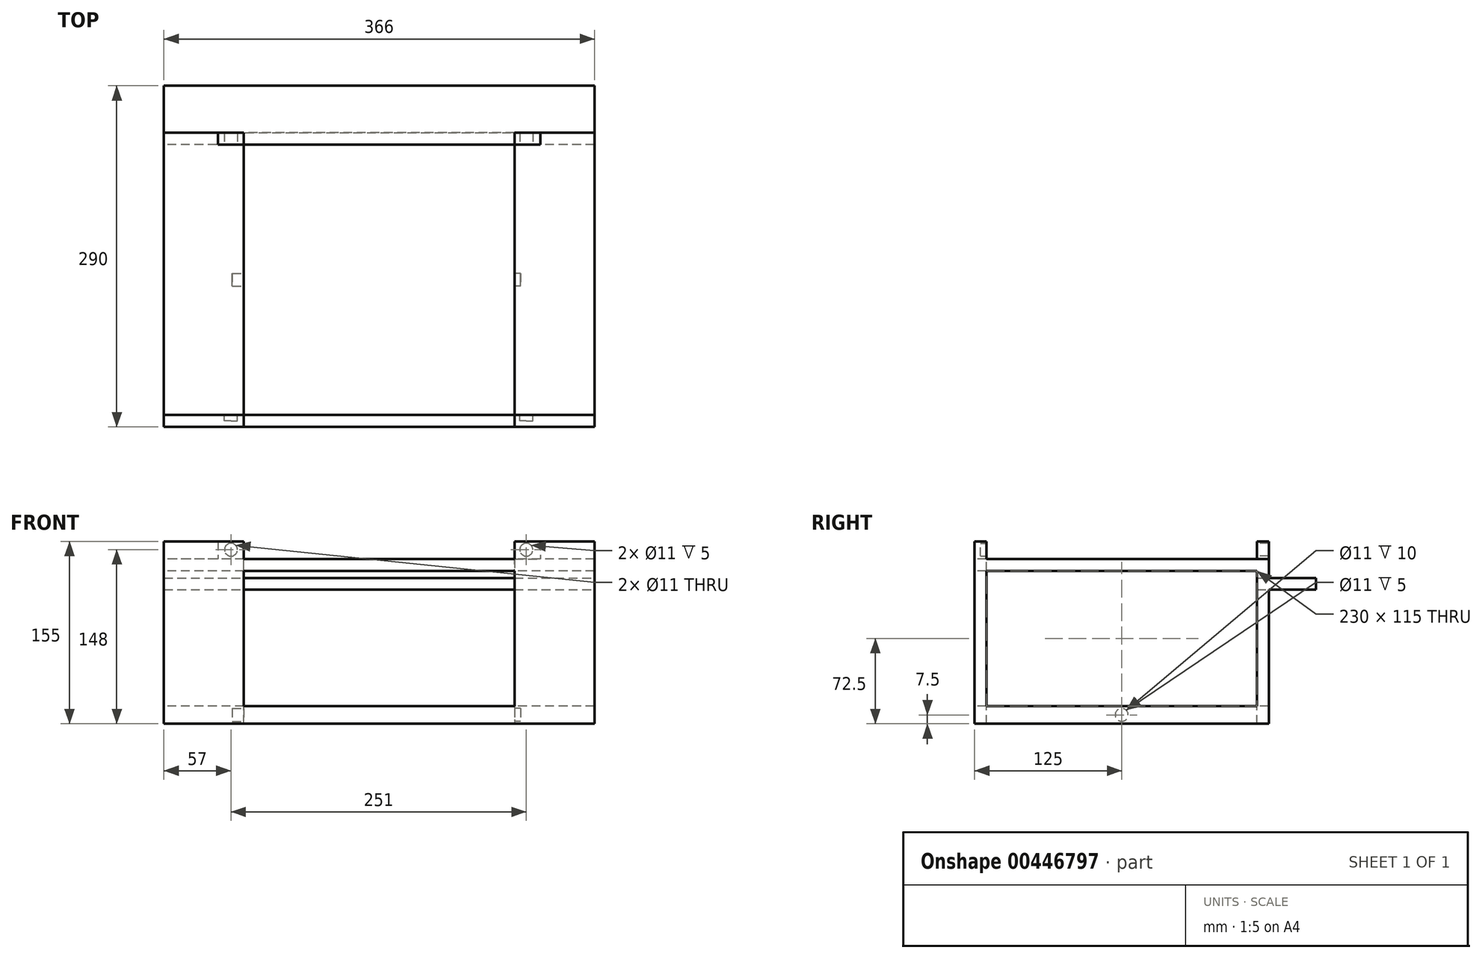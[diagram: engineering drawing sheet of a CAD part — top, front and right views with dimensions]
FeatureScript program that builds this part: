
annotation { "Feature Type Name" : "Feature", "Feature Type Description" : "" }
export const myFeature = defineFeature(function(context is Context, id is Id, definition is map)
    precondition{}
    {
        {
            var Q0;
            Q0=qCreatedBy(makeId("Top.planeOp"),FACE);
            var sketch = newSketch(context, id + "F0", { "sketchPlane" : qUnion([Q0])});
            skLineSegment(sketch, "E0.bottom", {"start": v(-183, 125) * mm, "end": v(183, 125) * mm});
            skLineSegment(sketch, "E0.top", {"start": v(-183, -125) * mm, "end": v(183, -125) * mm});
            skLineSegment(sketch, "E0.left", {"start": v(-183, 125) * mm, "end": v(-183, -125) * mm});
            skLineSegment(sketch, "E0.right", {"start": v(183, 125) * mm, "end": v(183, -125) * mm});
            skSolve(sketch);
        }
        {
            var Q0;
            Q0=qSketchRegion(id+"F0",true);
            extrude(context, id + "F1", {"entities" : qUnion([Q0]), "depth" : 155 * mm});
        }
        {
            var Q0;
            Q0=makeQuery(id+"F1.opExtrude","CAP_FACE",FACE,{"disambiguationData":[OSD([sQuery(id+"F0.wireOp",EDGE,"E0.bottom"),sQuery(id+"F0.wireOp",EDGE,"E0.top"),sQuery(id+"F0.wireOp",EDGE,"E0.left"),sQuery(id+"F0.wireOp",EDGE,"E0.right")])],"isStart":false});
            shell(context, id + "F2", {"entities" : qUnion([Q0]), "thickness" : 10 * mm});
        }
        {
            var Q0;
            Q0=makeQuery(id+"F2.opShell","OFFSET_FACE",FACE,{"disambiguationData":[OSD([sQuery(id+"F0.wireOp",EDGE,"E0.bottom"),sQuery(id+"F0.wireOp",EDGE,"E0.top"),sQuery(id+"F0.wireOp",EDGE,"E0.left"),sQuery(id+"F0.wireOp",EDGE,"E0.right")])]});
            var sketch = newSketch(context, id + "F3", { "sketchPlane" : qUnion([Q0])});
            skSolve(sketch);
        }
        {
            var Q0;
            Q0=qSketchRegion(id+"F3",true);
            var Q1;
            {var subQ0=sQuery(id+"F0.wireOp",EDGE,"E0.bottom");Q1=makeQuery(id+"F3.imprint","IMPRINT",FACE,{"disambiguationData":[TD([[makeQuery(id+"F3.imprint","IMPRINT",EDGE,{"derivedFrom":makeQuery(id+"F2.opShell","OFFSET_EDGE",EDGE,{"disambiguationData":[OSD([subQ0]),TDD([makeQuery(id+"F1.opExtrude","CAP_EDGE",EDGE,{"disambiguationData":[OSD([subQ0])],"isStart":true})])]})}),-1.0]])]});}
            extrude(context, id + "F4", {"entities" : qUnion([Q0, Q1]), "operationType" : NewBodyOperationType.REMOVE, "oppositeDirection" : true, "depth" : 25 * mm});
        }
        {
            var Q0;
            Q0=makeQuery(id+"F1.opExtrude","SWEPT_FACE",FACE,{"disambiguationData":[OSD([sQuery(id+"F0.wireOp",EDGE,"E0.top")])]});
            var sketch = newSketch(context, id + "F5", { "sketchPlane" : qUnion([Q0])});
            skLineSegment(sketch, "E1", {"start": v(0, 0) * mm, "end": v(0, 92.09) * mm});
            skLineSegment(sketch, "E2.bottom", {"start": v(-115, 130) * mm, "end": v(115, 130) * mm});
            skLineSegment(sketch, "E2.top", {"start": v(-115, 15) * mm, "end": v(115, 15) * mm});
            skLineSegment(sketch, "E2.left", {"start": v(-115, 130) * mm, "end": v(-115, 15) * mm});
            skLineSegment(sketch, "E2.right", {"start": v(115, 130) * mm, "end": v(115, 15) * mm});
            skLineSegment(sketch, "E3.bottom", {"start": v(-115, 155) * mm, "end": v(115, 155) * mm});
            skLineSegment(sketch, "E3.top", {"start": v(-115, 140) * mm, "end": v(115, 140) * mm});
            skLineSegment(sketch, "E3.left", {"start": v(-115, 155) * mm, "end": v(-115, 140) * mm});
            skLineSegment(sketch, "E3.right", {"start": v(115, 155) * mm, "end": v(115, 140) * mm});
            skSolve(sketch);
        }
        {
            var Q0;
            Q0=qSketchRegion(id+"F5",true);
            extrude(context, id + "F6", {"entities" : qUnion([Q0]), "operationType" : NewBodyOperationType.REMOVE, "oppositeDirection" : true, "depth" : 500 * mm});
        }
        {
            var Q0;
            Q0=makeQuery(id+"F1.opExtrude","SWEPT_FACE",FACE,{"disambiguationData":[OSD([sQuery(id+"F0.wireOp",EDGE,"E0.left")])]});
            var sketch = newSketch(context, id + "F7", { "sketchPlane" : qUnion([Q0])});
            skLineSegment(sketch, "E4", {"start": v(0, 0) * mm, "end": v(0, 112.83) * mm});
            skLineSegment(sketch, "E5.bottom", {"start": v(-115, 130) * mm, "end": v(115, 130) * mm});
            skLineSegment(sketch, "E5.top", {"start": v(-115, 15) * mm, "end": v(115, 15) * mm});
            skLineSegment(sketch, "E5.left", {"start": v(-115, 130) * mm, "end": v(-115, 15) * mm});
            skLineSegment(sketch, "E5.right", {"start": v(115, 130) * mm, "end": v(115, 15) * mm});
            skLineSegment(sketch, "E6.bottom", {"start": v(-125, 114) * mm, "end": v(-125, 114) * mm});
            skLineSegment(sketch, "E6.top", {"start": v(-125, 0) * mm, "end": v(-125, 0) * mm});
            skLineSegment(sketch, "E7.bottom", {"start": v(-125, 155) * mm, "end": v(115, 155) * mm});
            skLineSegment(sketch, "E7.top", {"start": v(-125, 140) * mm, "end": v(115, 140) * mm});
            skLineSegment(sketch, "E7.left", {"start": v(-125, 155) * mm, "end": v(-125, 140) * mm});
            skLineSegment(sketch, "E7.right", {"start": v(115, 155) * mm, "end": v(115, 140) * mm});
            skSolve(sketch);
        }
        {
            var Q0;
            Q0=makeQuery(id+"F7.imprint","IMPRINT",FACE,{"disambiguationData":[TD([[makeQuery(id+"F7.imprint","IMPRINT",EDGE,{"derivedFrom":sQuery(id+"F7.wireOp",EDGE,"E7.bottom")}),-1.0]])]});
            var Q1;
            Q1=makeQuery(id+"F7.imprint","IMPRINT",FACE,{"disambiguationData":[TD([[makeQuery(id+"F7.imprint","IMPRINT",EDGE,{"derivedFrom":sQuery(id+"F7.wireOp",EDGE,"E5.bottom")}),-1.0]])]});
            extrude(context, id + "F8", {"entities" : qUnion([Q0, Q1]), "operationType" : NewBodyOperationType.REMOVE, "oppositeDirection" : true, "depth" : 500 * mm});
        }
        {
            var Q0;
            Q0=makeQuery(id+"F1.opExtrude","SWEPT_FACE",FACE,{"disambiguationData":[OSD([sQuery(id+"F0.wireOp",EDGE,"E0.left")])]});
            var sketch = newSketch(context, id + "F9", { "sketchPlane" : qUnion([Q0])});
            skLineSegment(sketch, "E8.bottom", {"start": v(-115, 124) * mm, "end": v(-165, 124) * mm});
            skLineSegment(sketch, "E8.top", {"start": v(-115, 114) * mm, "end": v(-165, 114) * mm});
            skLineSegment(sketch, "E8.left", {"start": v(-115, 124) * mm, "end": v(-115, 114) * mm});
            skLineSegment(sketch, "E8.right", {"start": v(-165, 124) * mm, "end": v(-165, 114) * mm});
            skLineSegment(sketch, "E9.0", {"start": v(115, 155) * mm, "end": v(125, 155) * mm});
            skLineSegment(sketch, "E10.0", {"start": v(125, 155) * mm, "end": v(125, 0) * mm});
            skSolve(sketch);
        }
        {
            var Q0;
            Q0=qSketchRegion(id+"F9",true);
            var Q1;
            Q1=makeQuery(id+"F1.opExtrude","SWEPT_FACE",FACE,{"disambiguationData":[OSD([sQuery(id+"F0.wireOp",EDGE,"E0.right")])]});
            extrude(context, id + "F10", {"entities" : qUnion([Q0]), "operationType" : NewBodyOperationType.ADD, "endBound" : BoundingType.UP_TO_SURFACE, "oppositeDirection" : true, "endBoundEntityFace" : qUnion([Q1]), "depth" : 25 * mm});
        }
        {
            var Q0;
            {var subQ0=sQuery(id+"F0.wireOp",EDGE,"E0.bottom");var subQ1=makeQuery(id+"F1.opExtrude","SWEPT_FACE",FACE,{"disambiguationData":[OSD([subQ0])]});var subQ9=sQuery(id+"F9.wireOp",EDGE,"E8.bottom");Q0=makeQuery(id+"F10.boolean.opBoolean","SPLIT",FACE,{"disambiguationData":[TD([makeQuery(id+"F10.opExtrude","SWEPT_FACE",FACE,{"disambiguationData":[OSD([subQ9])]})])],"derivedFrom":subQ1});}
            var sketch = newSketch(context, id + "F11", { "sketchPlane" : qUnion([Q0])});
            skLineSegment(sketch, "E11.bottom", {"start": v(-115, 124) * mm, "end": v(115, 124) * mm});
            skLineSegment(sketch, "E11.top", {"start": v(-115, 150.02) * mm, "end": v(115, 150.02) * mm});
            skLineSegment(sketch, "E11.left", {"start": v(-115, 124) * mm, "end": v(-115, 150.02) * mm});
            skLineSegment(sketch, "E11.right", {"start": v(115, 124) * mm, "end": v(115, 150.02) * mm});
            skSolve(sketch);
        }
        {
            var Q0;
            {var subQ0=sQuery(id+"F11.wireOp",EDGE,"E11.bottom");Q0=makeQuery(id+"F11.imprint","IMPRINT",FACE,{"disambiguationData":[TD([[makeQuery(id+"F11.imprint","IMPRINT",EDGE,{"derivedFrom":subQ0}),1.0]])]});}
            var Q1;
            {var subQ1=sQuery(id+"F0.wireOp",EDGE,"E0.bottom");var subQ2=makeQuery(id+"F1.opExtrude","SWEPT_FACE",FACE,{"disambiguationData":[OSD([subQ1])]});var subQ3=makeQuery(id+"F6.boolean.opBoolean","INTERSECT",EDGE,{"derivedFrom":[subQ2,makeQuery(id+"F6.opExtrude","SWEPT_FACE",FACE,{"disambiguationData":[OSD([sQuery(id+"F5.wireOp",EDGE,"E2.bottom")])]})]});Q1=makeQuery(id+"F11.imprint","IMPRINT",FACE,{"disambiguationData":[TD([[makeQuery(id+"F11.imprint","IMPRINT",EDGE,{"derivedFrom":subQ3}),1.0]])]});}
            extrude(context, id + "F12", {"entities" : qUnion([Q0, Q1]), "operationType" : NewBodyOperationType.REMOVE, "oppositeDirection" : true, "depth" : 200 * mm});
        }
        {
            var Q0;
            {var subQ0=sQuery(id+"F0.wireOp",EDGE,"E0.right");var subQ2=sQuery(id+"F0.wireOp",EDGE,"E0.bottom");var subQ4=makeQuery(id+"F1.opExtrude","SWEPT_FACE",FACE,{"disambiguationData":[OSD([subQ2])]});Q0=makeQuery(id+"F12.boolean.opBoolean","SPLIT",FACE,{"disambiguationData":[TD([makeQuery(id+"F1.opExtrude","SWEPT_FACE",FACE,{"disambiguationData":[OSD([subQ0])]})])],"derivedFrom":makeQuery(id+"F8.boolean.opBoolean","MERGE",FACE,{"derivedFrom":[makeQuery(id+"F6.boolean.opBoolean","COPY",FACE,{"disambiguationData":[TD([subQ4])],"derivedFrom":makeQuery(id+"F6.opExtrude","SWEPT_FACE",FACE,{"disambiguationData":[OSD([sQuery(id+"F5.wireOp",EDGE,"E3.top")])]})}),makeQuery(id+"F8.opExtrude","SWEPT_FACE",FACE,{"disambiguationData":[OSD([sQuery(id+"F7.wireOp",EDGE,"E7.top")])]})]})});}
            var sketch = newSketch(context, id + "F13", { "sketchPlane" : qUnion([Q0])});
            skLineSegment(sketch, "E12.bottom", {"start": v(115, 115) * mm, "end": v(137, 115) * mm});
            skLineSegment(sketch, "E12.top", {"start": v(115, 125) * mm, "end": v(137, 125) * mm});
            skLineSegment(sketch, "E12.left", {"start": v(115, 115) * mm, "end": v(115, 125) * mm});
            skLineSegment(sketch, "E12.right", {"start": v(137, 115) * mm, "end": v(137, 125) * mm});
            skSolve(sketch);
        }
        {
            var Q0;
            Q0=makeQuery(id+"F13.imprint","IMPRINT",FACE,{"disambiguationData":[TD([[makeQuery(id+"F13.imprint","IMPRINT",EDGE,{"derivedFrom":sQuery(id+"F13.wireOp",EDGE,"E12.bottom")}),-1.0]])]});
            extrude(context, id + "F14", {"entities" : qUnion([Q0]), "operationType" : NewBodyOperationType.ADD, "depth" : 15 * mm});
        }
        {
            var Q0;
            {var subQ0=sQuery(id+"F0.wireOp",EDGE,"E0.bottom");var subQ3=makeQuery(id+"F1.opExtrude","SWEPT_FACE",FACE,{"disambiguationData":[OSD([subQ0])]});var subQ4=sQuery(id+"F0.wireOp",EDGE,"E0.left");Q0=makeQuery(id+"F12.boolean.opBoolean","SPLIT",FACE,{"disambiguationData":[TD([makeQuery(id+"F1.opExtrude","SWEPT_FACE",FACE,{"disambiguationData":[OSD([subQ4])]})])],"derivedFrom":makeQuery(id+"F8.boolean.opBoolean","MERGE",FACE,{"derivedFrom":[makeQuery(id+"F6.boolean.opBoolean","COPY",FACE,{"disambiguationData":[TD([subQ3])],"derivedFrom":makeQuery(id+"F6.opExtrude","SWEPT_FACE",FACE,{"disambiguationData":[OSD([sQuery(id+"F5.wireOp",EDGE,"E3.top")])]})}),makeQuery(id+"F8.opExtrude","SWEPT_FACE",FACE,{"disambiguationData":[OSD([sQuery(id+"F7.wireOp",EDGE,"E7.top")])]})]})});}
            var sketch = newSketch(context, id + "F15", { "sketchPlane" : qUnion([Q0])});
            skLineSegment(sketch, "E13.bottom", {"start": v(-115, 115) * mm, "end": v(-137, 115) * mm});
            skLineSegment(sketch, "E13.top", {"start": v(-115, 125) * mm, "end": v(-137, 125) * mm});
            skLineSegment(sketch, "E13.left", {"start": v(-115, 115) * mm, "end": v(-115, 125) * mm});
            skLineSegment(sketch, "E13.right", {"start": v(-137, 115) * mm, "end": v(-137, 125) * mm});
            skSolve(sketch);
        }
        {
            var Q0;
            Q0=makeQuery(id+"F15.imprint","IMPRINT",FACE,{"disambiguationData":[TD([[makeQuery(id+"F15.imprint","IMPRINT",EDGE,{"derivedFrom":sQuery(id+"F15.wireOp",EDGE,"E13.bottom")}),-1.0]])]});
            extrude(context, id + "F16", {"entities" : qUnion([Q0]), "operationType" : NewBodyOperationType.ADD, "depth" : 15 * mm});
        }
        {
            var Q0;
            {var subQ4=sQuery(id+"F0.wireOp",EDGE,"E0.right");Q0=makeQuery(id+"F8.boolean.opBoolean","SPLIT",FACE,{"disambiguationData":[TD([makeQuery(id+"F8.opExtrude","SWEPT_FACE",FACE,{"disambiguationData":[OSD([sQuery(id+"F7.wireOp",EDGE,"E5.bottom")])]})])],"derivedFrom":makeQuery(id+"F4.boolean.opBoolean","MERGE",FACE,{"derivedFrom":[makeQuery(id+"F2.opShell","OFFSET_FACE",FACE,{"disambiguationData":[OSD([subQ4])]}),makeQuery(id+"F4.opExtrude","SWEPT_FACE",FACE,{"disambiguationData":[OSD([subQ4])]})]})});}
            var Q1;
            {var subQ0=sQuery(id+"F0.wireOp",EDGE,"E0.top");Q1=makeQuery(id+"F6.boolean.opBoolean","COPY",FACE,{"disambiguationData":[TD([makeQuery(id+"F1.opExtrude","SWEPT_FACE",FACE,{"disambiguationData":[OSD([subQ0])]})])],"derivedFrom":makeQuery(id+"F6.opExtrude","SWEPT_FACE",FACE,{"disambiguationData":[OSD([sQuery(id+"F5.wireOp",EDGE,"E2.right")])]})});}
            extrude(context, id + "F17", {"entities" : qUnion([Q0]), "operationType" : NewBodyOperationType.ADD, "endBound" : BoundingType.UP_TO_SURFACE, "endBoundEntityFace" : qUnion([Q1]), "depth" : 25 * mm});
        }
        {
            var Q0;
            {var subQ4=sQuery(id+"F0.wireOp",EDGE,"E0.left");Q0=makeQuery(id+"F8.boolean.opBoolean","SPLIT",FACE,{"disambiguationData":[TD([makeQuery(id+"F8.opExtrude","SWEPT_FACE",FACE,{"disambiguationData":[OSD([sQuery(id+"F7.wireOp",EDGE,"E5.bottom")])]})])],"derivedFrom":makeQuery(id+"F4.boolean.opBoolean","MERGE",FACE,{"derivedFrom":[makeQuery(id+"F2.opShell","OFFSET_FACE",FACE,{"disambiguationData":[OSD([subQ4])]}),makeQuery(id+"F4.opExtrude","SWEPT_FACE",FACE,{"disambiguationData":[OSD([subQ4])]})]})});}
            var Q1;
            {var subQ0=sQuery(id+"F0.wireOp",EDGE,"E0.top");Q1=makeQuery(id+"F6.boolean.opBoolean","COPY",FACE,{"disambiguationData":[TD([makeQuery(id+"F1.opExtrude","SWEPT_FACE",FACE,{"disambiguationData":[OSD([subQ0])]})])],"derivedFrom":makeQuery(id+"F6.opExtrude","SWEPT_FACE",FACE,{"disambiguationData":[OSD([sQuery(id+"F5.wireOp",EDGE,"E2.left")])]})});}
            extrude(context, id + "F18", {"entities" : qUnion([Q0]), "operationType" : NewBodyOperationType.ADD, "endBound" : BoundingType.UP_TO_SURFACE, "endBoundEntityFace" : qUnion([Q1]), "depth" : 25 * mm});
        }
        {
            var Q0;
            {var subQ2=sQuery(id+"F0.wireOp",EDGE,"E0.right");Q0=makeQuery(id+"F8.boolean.opBoolean","SPLIT",FACE,{"disambiguationData":[TD([makeQuery(id+"F8.opExtrude","SWEPT_FACE",FACE,{"disambiguationData":[OSD([sQuery(id+"F7.wireOp",EDGE,"E5.top")])]})])],"derivedFrom":makeQuery(id+"F4.boolean.opBoolean","MERGE",FACE,{"derivedFrom":[makeQuery(id+"F2.opShell","OFFSET_FACE",FACE,{"disambiguationData":[OSD([subQ2])]}),makeQuery(id+"F4.opExtrude","SWEPT_FACE",FACE,{"disambiguationData":[OSD([subQ2])]})]})});}
            var Q1;
            {var subQ0=sQuery(id+"F0.wireOp",EDGE,"E0.top");Q1=makeQuery(id+"F6.boolean.opBoolean","COPY",FACE,{"disambiguationData":[TD([makeQuery(id+"F1.opExtrude","SWEPT_FACE",FACE,{"disambiguationData":[OSD([subQ0])]})])],"derivedFrom":makeQuery(id+"F6.opExtrude","SWEPT_FACE",FACE,{"disambiguationData":[OSD([sQuery(id+"F5.wireOp",EDGE,"E2.right")])]})});}
            extrude(context, id + "F19", {"entities" : qUnion([Q0]), "operationType" : NewBodyOperationType.ADD, "endBound" : BoundingType.UP_TO_SURFACE, "endBoundEntityFace" : qUnion([Q1]), "depth" : 25 * mm});
        }
        {
            var Q0;
            {var subQ2=sQuery(id+"F0.wireOp",EDGE,"E0.left");Q0=makeQuery(id+"F8.boolean.opBoolean","SPLIT",FACE,{"disambiguationData":[TD([makeQuery(id+"F8.opExtrude","SWEPT_FACE",FACE,{"disambiguationData":[OSD([sQuery(id+"F7.wireOp",EDGE,"E5.top")])]})])],"derivedFrom":makeQuery(id+"F4.boolean.opBoolean","MERGE",FACE,{"derivedFrom":[makeQuery(id+"F2.opShell","OFFSET_FACE",FACE,{"disambiguationData":[OSD([subQ2])]}),makeQuery(id+"F4.opExtrude","SWEPT_FACE",FACE,{"disambiguationData":[OSD([subQ2])]})]})});}
            var Q1;
            {var subQ0=sQuery(id+"F0.wireOp",EDGE,"E0.top");Q1=makeQuery(id+"F6.boolean.opBoolean","COPY",FACE,{"disambiguationData":[TD([makeQuery(id+"F1.opExtrude","SWEPT_FACE",FACE,{"disambiguationData":[OSD([subQ0])]})])],"derivedFrom":makeQuery(id+"F6.opExtrude","SWEPT_FACE",FACE,{"disambiguationData":[OSD([sQuery(id+"F5.wireOp",EDGE,"E2.left")])]})});}
            extrude(context, id + "F20", {"entities" : qUnion([Q0]), "operationType" : NewBodyOperationType.ADD, "endBound" : BoundingType.UP_TO_SURFACE, "endBoundEntityFace" : qUnion([Q1]), "depth" : 25 * mm});
        }
        {
            var Q0;
            {var subQ2=sQuery(id+"F13.wireOp",EDGE,"E12.right");var subQ3=sQuery(id+"F13.wireOp",EDGE,"E12.bottom");var subQ4=sQuery(id+"F0.wireOp",EDGE,"E0.bottom");var subQ6=makeQuery(id+"F2.opShell","OFFSET_FACE",FACE,{"disambiguationData":[OSD([subQ4])]});Q0=makeQuery(id+"F17.boolean.opBoolean","SPLIT",FACE,{"disambiguationData":[TD([makeQuery(id+"F14.opExtrude","SWEPT_FACE",FACE,{"disambiguationData":[OSD([subQ2])]})])],"derivedFrom":makeQuery(id+"F16.boolean.opBoolean","MERGE",FACE,{"derivedFrom":[makeQuery(id+"F14.boolean.opBoolean","MERGE",FACE,{"derivedFrom":[makeQuery(id+"F10.boolean.opBoolean","MERGE",FACE,{"derivedFrom":[makeQuery(id+"F8.boolean.opBoolean","MERGE",FACE,{"derivedFrom":[makeQuery(id+"F4.boolean.opBoolean","MERGE",FACE,{"derivedFrom":[subQ6],"fromTools":[makeQuery(id+"F4.opExtrude","SWEPT_FACE",FACE,{"disambiguationData":[OSD([subQ4])]})]})],"fromTools":[makeQuery(id+"F8.opExtrude","SWEPT_FACE",FACE,{"disambiguationData":[OSD([sQuery(id+"F7.wireOp",EDGE,"E5.left")])]})]}),makeQuery(id+"F10.opExtrude","SWEPT_FACE",FACE,{"disambiguationData":[OSD([sQuery(id+"F9.wireOp",EDGE,"E8.left")])]})]}),makeQuery(id+"F14.opExtrude","SWEPT_FACE",FACE,{"disambiguationData":[OSD([subQ3])]})]}),makeQuery(id+"F16.opExtrude","SWEPT_FACE",FACE,{"disambiguationData":[OSD([sQuery(id+"F15.wireOp",EDGE,"E13.bottom")])]})]})});}
            var sketch = newSketch(context, id + "F21", { "sketchPlane" : qUnion([Q0])});
            skCircle(sketch, "E14", {"center": v(125, 148) * mm, "radius": 5.5 * mm});
            skLineSegment(sketch, "E15.0.0", {"start": v(115, 155) * mm, "end": v(115, 140) * mm});
            skLineSegment(sketch, "E15.0.1", {"start": v(115, 140) * mm, "end": v(137, 140) * mm});
            skLineSegment(sketch, "E15.0.2", {"start": v(137, 140) * mm, "end": v(137, 155) * mm});
            skLineSegment(sketch, "E15.0.3", {"start": v(137, 155) * mm, "end": v(115, 155) * mm});
            skSolve(sketch);
        }
        {
            var Q0;
            Q0=makeQuery(id+"F21.imprint","IMPRINT",FACE,{"disambiguationData":[TD([[makeQuery(id+"F21.imprint","IMPRINT",EDGE,{"derivedFrom":sQuery(id+"F21.wireOp",EDGE,"E14")}),1.0]])]});
            extrude(context, id + "F22", {"entities" : qUnion([Q0]), "operationType" : NewBodyOperationType.REMOVE, "depth" : 235 * mm});
        }
        {
            var Q0;
            {var subQ2=sQuery(id+"F0.wireOp",EDGE,"E0.bottom");var subQ4=makeQuery(id+"F2.opShell","OFFSET_FACE",FACE,{"disambiguationData":[OSD([subQ2])]});var subQ6=sQuery(id+"F15.wireOp",EDGE,"E13.right");var subQ7=makeQuery(id+"F16.opExtrude","SWEPT_FACE",FACE,{"disambiguationData":[OSD([subQ6])]});var subQ8=sQuery(id+"F15.wireOp",EDGE,"E13.bottom");var subQ14=sQuery(id+"F0.wireOp",EDGE,"E0.left");var subQ21=sQuery(id+"F9.wireOp",EDGE,"E8.left");var subQ26=makeQuery(id+"F8.opExtrude","SWEPT_FACE",FACE,{"disambiguationData":[OSD([sQuery(id+"F7.wireOp",EDGE,"E5.left")])]});var subQ30=makeQuery(id+"F1.opExtrude","SWEPT_FACE",FACE,{"disambiguationData":[OSD([subQ14])]});Q0=makeQuery(id+"F18.boolean.opBoolean","SPLIT",FACE,{"disambiguationData":[TD([subQ7])],"derivedFrom":makeQuery(id+"F17.boolean.opBoolean","SPLIT",FACE,{"disambiguationData":[TD([subQ30])],"derivedFrom":makeQuery(id+"F16.boolean.opBoolean","MERGE",FACE,{"derivedFrom":[makeQuery(id+"F14.boolean.opBoolean","MERGE",FACE,{"derivedFrom":[makeQuery(id+"F10.boolean.opBoolean","MERGE",FACE,{"derivedFrom":[makeQuery(id+"F8.boolean.opBoolean","MERGE",FACE,{"derivedFrom":[makeQuery(id+"F4.boolean.opBoolean","MERGE",FACE,{"derivedFrom":[subQ4],"fromTools":[makeQuery(id+"F4.opExtrude","SWEPT_FACE",FACE,{"disambiguationData":[OSD([subQ2])]})]})],"fromTools":[subQ26]}),makeQuery(id+"F10.opExtrude","SWEPT_FACE",FACE,{"disambiguationData":[OSD([subQ21])]})]}),makeQuery(id+"F14.opExtrude","SWEPT_FACE",FACE,{"disambiguationData":[OSD([sQuery(id+"F13.wireOp",EDGE,"E12.bottom")])]})]}),makeQuery(id+"F16.opExtrude","SWEPT_FACE",FACE,{"disambiguationData":[OSD([subQ8])]})]})})});}
            var sketch = newSketch(context, id + "F23", { "sketchPlane" : qUnion([Q0])});
            skCircle(sketch, "E16", {"center": v(-126, 148) * mm, "radius": 5.5 * mm});
            skPoint(sketch, "E16.centerSnap0", {"position": v(-126, 155) * mm});
            skLineSegment(sketch, "E17.0.0", {"start": v(-137, 140) * mm, "end": v(-115, 140) * mm});
            skLineSegment(sketch, "E17.0.1", {"start": v(-115, 140) * mm, "end": v(-115, 155) * mm});
            skLineSegment(sketch, "E17.0.2", {"start": v(-115, 155) * mm, "end": v(-137, 155) * mm});
            skLineSegment(sketch, "E17.0.3", {"start": v(-137, 155) * mm, "end": v(-137, 140) * mm});
            skSolve(sketch);
        }
        {
            var Q0;
            Q0=makeQuery(id+"F23.imprint","IMPRINT",FACE,{"disambiguationData":[TD([[makeQuery(id+"F23.imprint","IMPRINT",EDGE,{"derivedFrom":sQuery(id+"F23.wireOp",EDGE,"E16")}),1.0]])]});
            extrude(context, id + "F24", {"entities" : qUnion([Q0]), "operationType" : NewBodyOperationType.REMOVE, "oppositeDirection" : true, "depth" : 25 * mm});
        }
        {
            var Q0;
            Q0=makeQuery(id+"F19.opExtrude","CAP_FACE",FACE,{"disambiguationData":[OSD([sQuery(id+"F0.wireOp",EDGE,"E0.right")])],"isStart":false});
            var sketch = newSketch(context, id + "F25", { "sketchPlane" : qUnion([Q0])});
            skCircle(sketch, "E18", {"center": v(0, 7.5) * mm, "radius": 5.5 * mm});
            skLineSegment(sketch, "E19.0.0", {"start": v(-125, 140) * mm, "end": v(-125, 124) * mm});
            skLineSegment(sketch, "E19.0.1", {"start": v(-125, 124) * mm, "end": v(-165, 124) * mm});
            skLineSegment(sketch, "E19.0.2", {"start": v(-165, 124) * mm, "end": v(-165, 114) * mm});
            skLineSegment(sketch, "E19.0.3", {"start": v(-165, 114) * mm, "end": v(-125, 114) * mm});
            skLineSegment(sketch, "E19.0.4", {"start": v(-125, 114) * mm, "end": v(-125, 0) * mm});
            skLineSegment(sketch, "E19.0.5", {"start": v(-125, 0) * mm, "end": v(125, 0) * mm});
            skLineSegment(sketch, "E19.0.6", {"start": v(125, 0) * mm, "end": v(125, 155) * mm});
            skLineSegment(sketch, "E19.0.7", {"start": v(125, 155) * mm, "end": v(115, 155) * mm});
            skLineSegment(sketch, "E19.0.8", {"start": v(115, 155) * mm, "end": v(115, 140) * mm});
            skLineSegment(sketch, "E19.0.9", {"start": v(115, 140) * mm, "end": v(-125, 140) * mm});
            skSolve(sketch);
        }
        {
            var Q0;
            Q0=makeQuery(id+"F25.imprint","IMPRINT",FACE,{"disambiguationData":[TD([[makeQuery(id+"F25.imprint","IMPRINT",EDGE,{"derivedFrom":sQuery(id+"F25.wireOp",EDGE,"E18")}),1.0]])]});
            extrude(context, id + "F26", {"entities" : qUnion([Q0]), "operationType" : NewBodyOperationType.REMOVE, "depth" : 240 * mm});
        }
        {
            var Q0;
            Q0=makeQuery(id+"F22.boolean.opBoolean","COPY",FACE,{"derivedFrom":makeQuery(id+"F22.opExtrude","CAP_FACE",FACE,{"disambiguationData":[OSD([sQuery(id+"F21.wireOp",EDGE,"E14")])],"isStart":false})});
            extrude(context, id + "F27", {"entities" : qUnion([Q0]), "operationType" : NewBodyOperationType.REMOVE, "depth" : 260 * mm});
        }
        {
            var Q0;
            {var subQ2=sQuery(id+"F0.wireOp",EDGE,"E0.bottom");var subQ4=makeQuery(id+"F2.opShell","OFFSET_FACE",FACE,{"disambiguationData":[OSD([subQ2])]});var subQ6=sQuery(id+"F15.wireOp",EDGE,"E13.right");var subQ7=makeQuery(id+"F16.opExtrude","SWEPT_FACE",FACE,{"disambiguationData":[OSD([subQ6])]});var subQ8=sQuery(id+"F15.wireOp",EDGE,"E13.bottom");var subQ14=sQuery(id+"F0.wireOp",EDGE,"E0.left");var subQ21=sQuery(id+"F9.wireOp",EDGE,"E8.left");var subQ26=makeQuery(id+"F8.opExtrude","SWEPT_FACE",FACE,{"disambiguationData":[OSD([sQuery(id+"F7.wireOp",EDGE,"E5.left")])]});var subQ30=makeQuery(id+"F1.opExtrude","SWEPT_FACE",FACE,{"disambiguationData":[OSD([subQ14])]});Q0=makeQuery(id+"F18.boolean.opBoolean","SPLIT",FACE,{"disambiguationData":[TD([subQ7])],"derivedFrom":makeQuery(id+"F17.boolean.opBoolean","SPLIT",FACE,{"disambiguationData":[TD([subQ30])],"derivedFrom":makeQuery(id+"F16.boolean.opBoolean","MERGE",FACE,{"derivedFrom":[makeQuery(id+"F14.boolean.opBoolean","MERGE",FACE,{"derivedFrom":[makeQuery(id+"F10.boolean.opBoolean","MERGE",FACE,{"derivedFrom":[makeQuery(id+"F8.boolean.opBoolean","MERGE",FACE,{"derivedFrom":[makeQuery(id+"F4.boolean.opBoolean","MERGE",FACE,{"derivedFrom":[subQ4],"fromTools":[makeQuery(id+"F4.opExtrude","SWEPT_FACE",FACE,{"disambiguationData":[OSD([subQ2])]})]})],"fromTools":[subQ26]}),makeQuery(id+"F10.opExtrude","SWEPT_FACE",FACE,{"disambiguationData":[OSD([subQ21])]})]}),makeQuery(id+"F14.opExtrude","SWEPT_FACE",FACE,{"disambiguationData":[OSD([sQuery(id+"F13.wireOp",EDGE,"E12.bottom")])]})]}),makeQuery(id+"F16.opExtrude","SWEPT_FACE",FACE,{"disambiguationData":[OSD([subQ8])]})]})})});}
            var sketch = newSketch(context, id + "F28", { "sketchPlane" : qUnion([Q0])});
            skCircle(sketch, "E20.0", {"center": v(-126, 148) * mm, "radius": 5.5 * mm});
            skSolve(sketch);
        }
        {
            var Q0;
            Q0=makeQuery(id+"F28.imprint","IMPRINT",FACE,{"disambiguationData":[TD([[makeQuery(id+"F28.imprint","IMPRINT",EDGE,{"derivedFrom":sQuery(id+"F28.wireOp",EDGE,"E20.0")}),1.0]])]});
            extrude(context, id + "F29", {"entities" : qUnion([Q0]), "operationType" : NewBodyOperationType.REMOVE, "depth" : 235 * mm});
        }
        {
            var Q0;
            Q0=makeQuery(id+"F19.opExtrude","CAP_FACE",FACE,{"disambiguationData":[OSD([sQuery(id+"F0.wireOp",EDGE,"E0.right")])],"isStart":false});
            var sketch = newSketch(context, id + "F30", { "sketchPlane" : qUnion([Q0])});
            skCircle(sketch, "E21", {"center": v(0, 7.5) * mm, "radius": 5.5 * mm});
            skSolve(sketch);
        }
        {
            var Q0;
            Q0=qSketchRegion(id+"F30",true);
            extrude(context, id + "F31", {"entities" : qUnion([Q0]), "operationType" : NewBodyOperationType.REMOVE, "oppositeDirection" : true, "depth" : 5 * mm});
        }
    });
